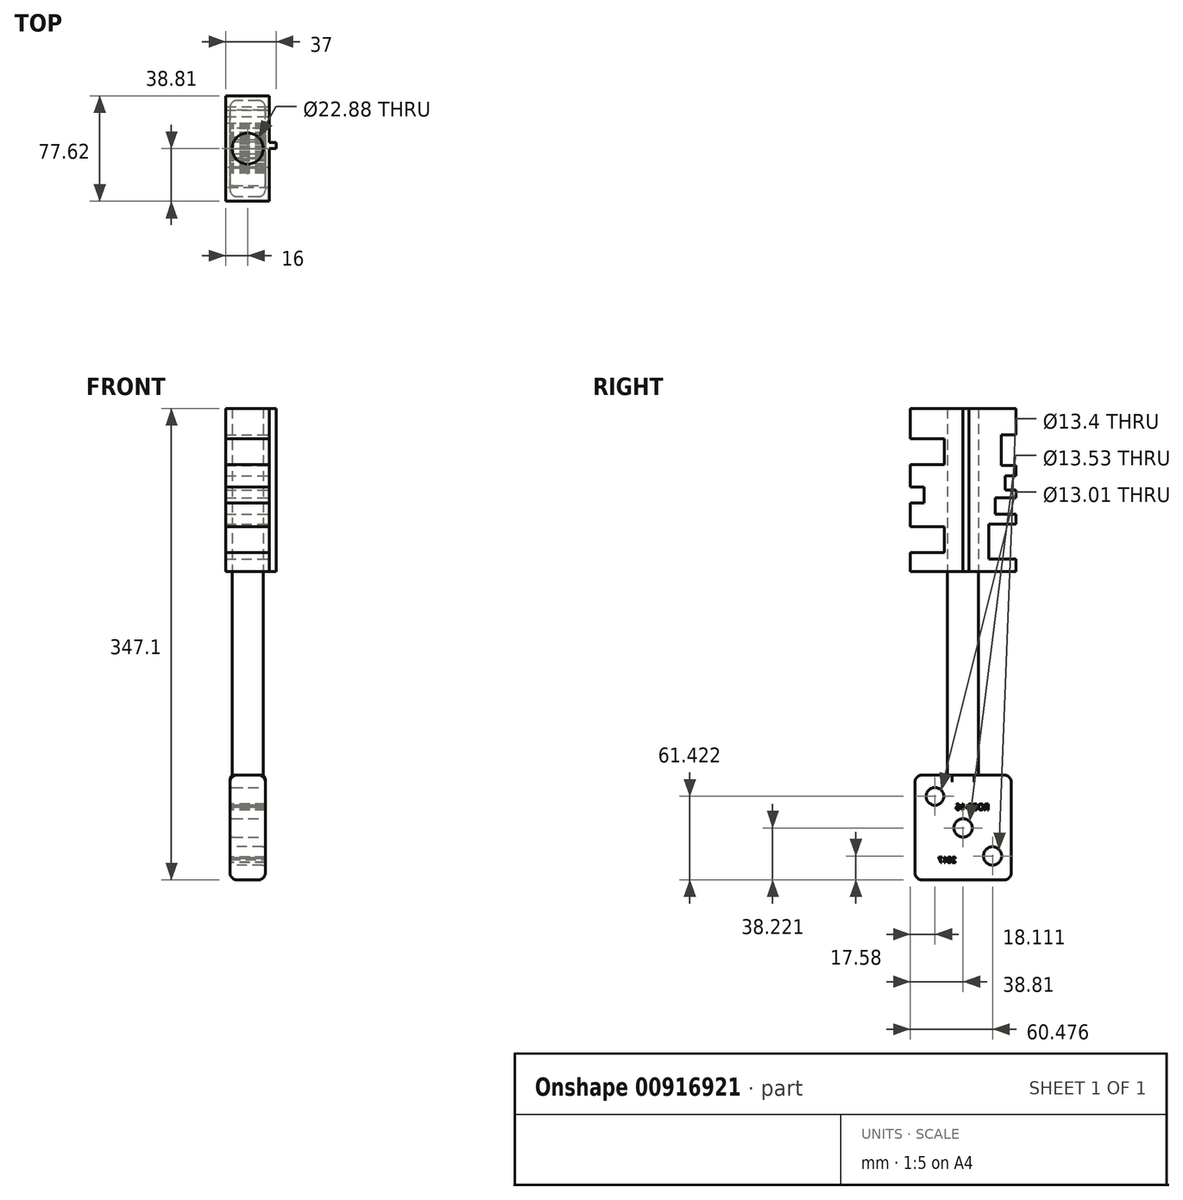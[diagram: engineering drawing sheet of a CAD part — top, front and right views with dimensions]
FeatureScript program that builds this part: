
annotation { "Feature Type Name" : "Feature", "Feature Type Description" : "" }
export const myFeature = defineFeature(function(context is Context, id is Id, definition is map)
    precondition{}
    {
        {
            var Q0;
            Q0=qCreatedBy(makeId("Top.planeOp"),FACE);
            var sketch = newSketch(context, id + "F0", { "sketchPlane" : qUnion([Q0])});
            skCircle(sketch, "E0", {"center": v(0, 0) * mm, "radius": 11.44 * mm});
            skSolve(sketch);
        }
        {
            var Q0;
            Q0=makeQuery(id+"F0.imprint","IMPRINT",FACE,{"disambiguationData":[TD([[makeQuery(id+"F0.imprint","IMPRINT",EDGE,{"derivedFrom":sQuery(id+"F0.wireOp",EDGE,"E0")}),1.0]])]});
            extrude(context, id + "F1", {"entities" : qUnion([Q0]), "depth" : 150 * mm, "offsetDistance" : 25 * mm});
        }
        {
            var Q0;
            Q0=makeQuery(id+"F1.opExtrude","CAP_FACE",FACE,{"disambiguationData":[OSD([sQuery(id+"F0.wireOp",EDGE,"E0")])],"isStart":false});
            var sketch = newSketch(context, id + "F2", { "sketchPlane" : qUnion([Q0])});
            skLineSegment(sketch, "E1.bottom", {"start": v(-16, 38.81) * mm, "end": v(16, 38.81) * mm});
            skLineSegment(sketch, "E1.top", {"start": v(-16, -38.81) * mm, "end": v(16, -38.81) * mm});
            skLineSegment(sketch, "E1.left", {"start": v(-16, 38.81) * mm, "end": v(-16, -38.81) * mm});
            skLineSegment(sketch, "E1.right", {"start": v(16, 38.81) * mm, "end": v(16, -38.81) * mm});
            skPoint(sketch, "E1.middle", {"position": v(0, 0) * mm});
            skSolve(sketch);
        }
        {
            var Q0;
            Q0=makeQuery(id+"F2.imprint","IMPRINT",FACE,{"disambiguationData":[TD([[makeQuery(id+"F2.imprint","IMPRINT",EDGE,{"derivedFrom":sQuery(id+"F2.wireOp",EDGE,"E1.bottom")}),-1.0]])]});
            extrude(context, id + "F3", {"entities" : qUnion([Q0]), "depth" : 120 * mm, "offsetDistance" : 25 * mm});
        }
        {
            var Q0;
            Q0=makeQuery(id+"F3.opExtrude","SWEPT_FACE",FACE,{"disambiguationData":[OSD([sQuery(id+"F2.wireOp",EDGE,"E1.top")])]});
            var sketch = newSketch(context, id + "F4", { "sketchPlane" : qUnion([Q0])});
            skLineSegment(sketch, "E2.bottom", {"start": v(16, 182.75) * mm, "end": v(-16, 182.75) * mm});
            skLineSegment(sketch, "E2.top", {"start": v(16, 163.99) * mm, "end": v(-16, 163.99) * mm});
            skLineSegment(sketch, "E2.left", {"start": v(16, 182.75) * mm, "end": v(16, 163.99) * mm});
            skLineSegment(sketch, "E2.right", {"start": v(-16, 182.75) * mm, "end": v(-16, 163.99) * mm});
            skPoint(sketch, "E2.middle", {"position": v(0, 173.37) * mm});
            skSolve(sketch);
        }
        {
            var Q0;
            Q0=makeQuery(id+"F4.imprint","IMPRINT",FACE,{"disambiguationData":[TD([[makeQuery(id+"F4.imprint","IMPRINT",EDGE,{"derivedFrom":sQuery(id+"F4.wireOp",EDGE,"E2.bottom")}),1.0]])]});
            extrude(context, id + "F5", {"entities" : qUnion([Q0]), "operationType" : NewBodyOperationType.REMOVE, "oppositeDirection" : true, "depth" : 25 * mm, "offsetDistance" : 25 * mm});
        }
        {
            var Q0;
            {var subQ2=sQuery(id+"F2.wireOp",EDGE,"E1.top");Q0=makeQuery(id+"F5.boolean.opBoolean","SPLIT",FACE,{"disambiguationData":[TD([makeQuery(id+"F5.opExtrude","SWEPT_FACE",FACE,{"disambiguationData":[OSD([sQuery(id+"F4.wireOp",EDGE,"E2.bottom")])]})])],"derivedFrom":makeQuery(id+"F3.opExtrude","SWEPT_FACE",FACE,{"disambiguationData":[OSD([subQ2])]})});}
            var sketch = newSketch(context, id + "F6", { "sketchPlane" : qUnion([Q0])});
            skLineSegment(sketch, "E3.bottom", {"start": v(16, 247.82) * mm, "end": v(-16, 247.82) * mm});
            skLineSegment(sketch, "E3.top", {"start": v(16, 228.54) * mm, "end": v(-16, 228.54) * mm});
            skLineSegment(sketch, "E3.left", {"start": v(16, 247.82) * mm, "end": v(16, 228.54) * mm});
            skLineSegment(sketch, "E3.right", {"start": v(-16, 247.82) * mm, "end": v(-16, 228.54) * mm});
            skPoint(sketch, "E3.middle", {"position": v(0, 238.18) * mm});
            skSolve(sketch);
        }
        {
            var Q0;
            Q0=makeQuery(id+"F6.imprint","IMPRINT",FACE,{"disambiguationData":[TD([[makeQuery(id+"F6.imprint","IMPRINT",EDGE,{"derivedFrom":sQuery(id+"F6.wireOp",EDGE,"E3.bottom")}),1.0]])]});
            extrude(context, id + "F7", {"entities" : qUnion([Q0]), "operationType" : NewBodyOperationType.REMOVE, "oppositeDirection" : true, "depth" : 25 * mm, "offsetDistance" : 25 * mm});
        }
        {
            var Q0;
            {var subQ2=makeQuery(id+"F5.opExtrude","SWEPT_FACE",FACE,{"disambiguationData":[OSD([sQuery(id+"F4.wireOp",EDGE,"E2.bottom")])]});var subQ5=sQuery(id+"F2.wireOp",EDGE,"E1.top");Q0=makeQuery(id+"F7.boolean.opBoolean","SPLIT",FACE,{"disambiguationData":[TD([makeQuery(id+"F5.boolean.opBoolean","COPY",FACE,{"derivedFrom":subQ2})])],"derivedFrom":makeQuery(id+"F5.boolean.opBoolean","SPLIT",FACE,{"disambiguationData":[TD([subQ2])],"derivedFrom":makeQuery(id+"F3.opExtrude","SWEPT_FACE",FACE,{"disambiguationData":[OSD([subQ5])]})})});}
            var sketch = newSketch(context, id + "F8", { "sketchPlane" : qUnion([Q0])});
            skLineSegment(sketch, "E4.bottom", {"start": v(16, 200.25) * mm, "end": v(-16, 200.25) * mm});
            skLineSegment(sketch, "E4.top", {"start": v(16, 212.16) * mm, "end": v(-16, 212.16) * mm});
            skLineSegment(sketch, "E4.left", {"start": v(16, 200.25) * mm, "end": v(16, 212.16) * mm});
            skLineSegment(sketch, "E4.right", {"start": v(-16, 200.25) * mm, "end": v(-16, 212.16) * mm});
            skPoint(sketch, "E4.middle", {"position": v(0, 206.2) * mm});
            skSolve(sketch);
        }
        {
            var Q0;
            Q0=makeQuery(id+"F8.imprint","IMPRINT",FACE,{"disambiguationData":[TD([[makeQuery(id+"F8.imprint","IMPRINT",EDGE,{"derivedFrom":sQuery(id+"F8.wireOp",EDGE,"E4.bottom")}),-1.0]])]});
            extrude(context, id + "F9", {"entities" : qUnion([Q0]), "operationType" : NewBodyOperationType.REMOVE, "oppositeDirection" : true, "depth" : 10 * mm, "offsetDistance" : 25 * mm});
        }
        {
            var Q0;
            Q0=qCreatedBy(makeId("Top.planeOp"),FACE);
            var sketch = newSketch(context, id + "F10", { "sketchPlane" : qUnion([Q0])});
            skLineSegment(sketch, "E5.bottom", {"start": v(12.98, 35.37) * mm, "end": v(-12.98, 35.37) * mm});
            skLineSegment(sketch, "E5.top", {"start": v(12.98, -35.37) * mm, "end": v(-12.98, -35.37) * mm});
            skLineSegment(sketch, "E5.left", {"start": v(12.98, 35.37) * mm, "end": v(12.98, -35.37) * mm});
            skLineSegment(sketch, "E5.right", {"start": v(-12.98, 35.37) * mm, "end": v(-12.98, -35.37) * mm});
            skPoint(sketch, "E5.middle", {"position": v(0, 0) * mm});
            skSolve(sketch);
        }
        {
            var Q0;
            Q0=makeQuery(id+"F10.imprint","IMPRINT",FACE,{"disambiguationData":[TD([[makeQuery(id+"F10.imprint","IMPRINT",EDGE,{"derivedFrom":sQuery(id+"F10.wireOp",EDGE,"E5.bottom")}),1.0]])]});
            extrude(context, id + "F11", {"entities" : qUnion([Q0]), "operationType" : NewBodyOperationType.ADD, "oppositeDirection" : true, "depth" : 77.1 * mm, "offsetDistance" : 25 * mm});
        }
        {
            var Q0;
            Q0=makeQuery(id+"F11.opExtrude","CAP_FACE",FACE,{"disambiguationData":[OSD([sQuery(id+"F10.wireOp",EDGE,"E5.bottom"),sQuery(id+"F10.wireOp",EDGE,"E5.top"),sQuery(id+"F10.wireOp",EDGE,"E5.left"),sQuery(id+"F10.wireOp",EDGE,"E5.right")])],"isStart":false});
            fillet(context, id + "F12", {"entities" : qUnion([Q0]), "radius" : 5 * mm, "tangentPropagation" : true, "allowEdgeOverflow" : false});
        }
        {
            var Q0;
            Q0=makeQuery(id+"F11.opExtrude","SWEPT_FACE",FACE,{"disambiguationData":[OSD([sQuery(id+"F10.wireOp",EDGE,"E5.left")])]});
            var Q1;
            Q1=makeQuery(id+"F11.opExtrude","SWEPT_FACE",FACE,{"disambiguationData":[OSD([sQuery(id+"F10.wireOp",EDGE,"E5.bottom")])]});
            var Q2;
            Q2=makeQuery(id+"F11.opExtrude","SWEPT_FACE",FACE,{"disambiguationData":[OSD([sQuery(id+"F10.wireOp",EDGE,"E5.right")])]});
            var Q3;
            Q3=makeQuery(id+"F11.opExtrude","SWEPT_FACE",FACE,{"disambiguationData":[OSD([sQuery(id+"F10.wireOp",EDGE,"E5.top")])]});
            fillet(context, id + "F13", {"entities" : qUnion([Q0, Q1, Q2, Q3]), "radius" : 5 * mm, "tangentPropagation" : true, "allowEdgeOverflow" : false});
        }
        {
            var Q0;
            Q0=makeQuery(id+"F11.opExtrude","SWEPT_FACE",FACE,{"disambiguationData":[OSD([sQuery(id+"F10.wireOp",EDGE,"E5.right")])]});
            var sketch = newSketch(context, id + "F14", { "sketchPlane" : qUnion([Q0])});
            skCircle(sketch, "E6", {"center": v(-21.67, -59.52) * mm, "radius": 6.7 * mm});
            skSolve(sketch);
        }
        {
            var Q0;
            Q0=makeQuery(id+"F14.imprint","IMPRINT",FACE,{"disambiguationData":[TD([[makeQuery(id+"F14.imprint","IMPRINT",EDGE,{"derivedFrom":sQuery(id+"F14.wireOp",EDGE,"E6")}),1.0]])]});
            extrude(context, id + "F15", {"entities" : qUnion([Q0]), "operationType" : NewBodyOperationType.REMOVE, "oppositeDirection" : true, "depth" : 100000 * mm, "offsetDistance" : 25 * mm});
        }
        {
            var Q0;
            Q0=makeQuery(id+"F11.opExtrude","SWEPT_FACE",FACE,{"disambiguationData":[OSD([sQuery(id+"F10.wireOp",EDGE,"E5.left")])]});
            var sketch = newSketch(context, id + "F16", { "sketchPlane" : qUnion([Q0])});
            skCircle(sketch, "E7", {"center": v(0, -38.88) * mm, "radius": 6.77 * mm});
            skSolve(sketch);
        }
        {
            var Q0;
            Q0=makeQuery(id+"F16.imprint","IMPRINT",FACE,{"disambiguationData":[TD([[makeQuery(id+"F16.imprint","IMPRINT",EDGE,{"derivedFrom":sQuery(id+"F16.wireOp",EDGE,"E7")}),1.0]])]});
            extrude(context, id + "F17", {"entities" : qUnion([Q0]), "operationType" : NewBodyOperationType.REMOVE, "oppositeDirection" : true, "depth" : 100000 * mm, "offsetDistance" : 25 * mm});
        }
        {
            var Q0;
            Q0=makeQuery(id+"F11.opExtrude","SWEPT_FACE",FACE,{"disambiguationData":[OSD([sQuery(id+"F10.wireOp",EDGE,"E5.left")])]});
            var sketch = newSketch(context, id + "F18", { "sketchPlane" : qUnion([Q0])});
            skCircle(sketch, "E8", {"center": v(-20.7, -15.68) * mm, "radius": 6.5 * mm});
            skSolve(sketch);
        }
        {
            var Q0;
            Q0=makeQuery(id+"F18.imprint","IMPRINT",FACE,{"disambiguationData":[TD([[makeQuery(id+"F18.imprint","IMPRINT",EDGE,{"derivedFrom":sQuery(id+"F18.wireOp",EDGE,"E8")}),1.0]])]});
            extrude(context, id + "F19", {"entities" : qUnion([Q0]), "operationType" : NewBodyOperationType.REMOVE, "oppositeDirection" : true, "depth" : 100300 * mm, "offsetDistance" : 25 * mm});
        }
        {
            var Q0;
            Q0=makeQuery(id+"F11.opExtrude","SWEPT_FACE",FACE,{"disambiguationData":[OSD([sQuery(id+"F10.wireOp",EDGE,"E5.right")])]});
            var sketch = newSketch(context, id + "F20", { "sketchPlane" : qUnion([Q0])});
            skText(sketch, "E9", { "text": "ROB9-16", "fontName": "OpenSans-Regular.ttf"});
            skText(sketch, "E10", { "text": "2017", "fontName": "OpenSans-Regular.ttf"});
            const initialGuessF20  = {"E9": [-0.01917, -0.02555, 1, 0, 0.00434], "E10": [0.00512, -0.0645, 1, 0, 0.00416]};
            skSetInitialGuess(sketch, initialGuessF20);
            skSolve(sketch);
        }
        {
            var Q0;
            Q0 = qSketchRegion(id + "F20", true);
            extrude(context, id + "F21", {"entities" : qUnion([Q0]), "operationType" : NewBodyOperationType.REMOVE, "oppositeDirection" : true, "depth" : 100000 * mm, "offsetDistance" : 25 * mm});
        }
        {
            var Q0;
            Q0=makeQuery(id+"F3.opExtrude","SWEPT_FACE",FACE,{"disambiguationData":[OSD([sQuery(id+"F2.wireOp",EDGE,"E1.right")])]});
            var sketch = newSketch(context, id + "F22", { "sketchPlane" : qUnion([Q0])});
            skLineSegment(sketch, "E11.bottom", {"start": v(4.4, 270) * mm, "end": v(0, 270) * mm});
            skLineSegment(sketch, "E11.top", {"start": v(4.4, 150) * mm, "end": v(0, 150) * mm});
            skLineSegment(sketch, "E11.left", {"start": v(4.4, 270) * mm, "end": v(4.4, 150) * mm});
            skLineSegment(sketch, "E11.right", {"start": v(0, 270) * mm, "end": v(0, 150) * mm});
            skSolve(sketch);
        }
        {
            var Q0;
            Q0=makeQuery(id+"F22.imprint","IMPRINT",FACE,{"disambiguationData":[TD([[makeQuery(id+"F22.imprint","IMPRINT",EDGE,{"derivedFrom":sQuery(id+"F22.wireOp",EDGE,"E11.bottom")}),1.0]])]});
            extrude(context, id + "F23", {"entities" : qUnion([Q0]), "operationType" : NewBodyOperationType.ADD, "depth" : 5 * mm, "offsetDistance" : 25 * mm});
        }
        {
            var Q0;
            {var subQ0=sQuery(id+"F2.wireOp",EDGE,"E1.right");var subQ3=sQuery(id+"F2.wireOp",EDGE,"E1.bottom");Q0=makeQuery(id+"F23.boolean.opBoolean","SPLIT",FACE,{"disambiguationData":[TD([makeQuery(id+"F3.opExtrude","SWEPT_FACE",FACE,{"disambiguationData":[OSD([subQ3])]})])],"derivedFrom":makeQuery(id+"F3.opExtrude","SWEPT_FACE",FACE,{"disambiguationData":[OSD([subQ0])]})});}
            var sketch = newSketch(context, id + "F24", { "sketchPlane" : qUnion([Q0])});
            skLineSegment(sketch, "E12.bottom", {"start": v(38.81, 250.4) * mm, "end": v(28.19, 250.4) * mm});
            skLineSegment(sketch, "E12.top", {"start": v(38.81, 228.1) * mm, "end": v(28.19, 228.1) * mm});
            skLineSegment(sketch, "E12.left", {"start": v(38.81, 250.4) * mm, "end": v(38.81, 228.1) * mm});
            skLineSegment(sketch, "E12.right", {"start": v(28.19, 250.4) * mm, "end": v(28.19, 228.1) * mm});
            skSolve(sketch);
        }
        {
            var Q0;
            Q0=makeQuery(id+"F24.imprint","IMPRINT",FACE,{"disambiguationData":[TD([[makeQuery(id+"F24.imprint","IMPRINT",EDGE,{"derivedFrom":sQuery(id+"F24.wireOp",EDGE,"E12.bottom")}),1.0]])]});
            extrude(context, id + "F25", {"entities" : qUnion([Q0]), "operationType" : NewBodyOperationType.REMOVE, "oppositeDirection" : true, "depth" : 100300 * mm, "offsetDistance" : 25 * mm});
        }
        {
            var Q0;
            {var subQ0=sQuery(id+"F2.wireOp",EDGE,"E1.right");var subQ3=sQuery(id+"F2.wireOp",EDGE,"E1.bottom");Q0=makeQuery(id+"F23.boolean.opBoolean","SPLIT",FACE,{"disambiguationData":[TD([makeQuery(id+"F3.opExtrude","SWEPT_FACE",FACE,{"disambiguationData":[OSD([subQ3])]})])],"derivedFrom":makeQuery(id+"F3.opExtrude","SWEPT_FACE",FACE,{"disambiguationData":[OSD([subQ0])]})});}
            var sketch = newSketch(context, id + "F26", { "sketchPlane" : qUnion([Q0])});
            skPoint(sketch, "E13.oppositeSnap0", {"position": v(4.4, 210) * mm});
            skLineSegment(sketch, "E13.bottom", {"start": v(38.81, 220.4) * mm, "end": v(30.93, 220.4) * mm});
            skLineSegment(sketch, "E13.top", {"start": v(38.81, 210) * mm, "end": v(30.93, 210) * mm});
            skLineSegment(sketch, "E13.left", {"start": v(38.81, 220.4) * mm, "end": v(38.81, 210) * mm});
            skLineSegment(sketch, "E13.right", {"start": v(30.93, 220.4) * mm, "end": v(30.93, 210) * mm});
            skSolve(sketch);
        }
        {
            var Q0;
            Q0=makeQuery(id+"F26.imprint","IMPRINT",FACE,{"disambiguationData":[TD([[makeQuery(id+"F26.imprint","IMPRINT",EDGE,{"derivedFrom":sQuery(id+"F26.wireOp",EDGE,"E13.bottom")}),1.0]])]});
            extrude(context, id + "F27", {"entities" : qUnion([Q0]), "operationType" : NewBodyOperationType.REMOVE, "oppositeDirection" : true, "depth" : 90 * mm, "offsetDistance" : 25 * mm});
        }
        {
            var Q0;
            {var subQ0=sQuery(id+"F2.wireOp",EDGE,"E1.right");var subQ3=sQuery(id+"F2.wireOp",EDGE,"E1.bottom");Q0=makeQuery(id+"F23.boolean.opBoolean","SPLIT",FACE,{"disambiguationData":[TD([makeQuery(id+"F3.opExtrude","SWEPT_FACE",FACE,{"disambiguationData":[OSD([subQ3])]})])],"derivedFrom":makeQuery(id+"F3.opExtrude","SWEPT_FACE",FACE,{"disambiguationData":[OSD([subQ0])]})});}
            var sketch = newSketch(context, id + "F28", { "sketchPlane" : qUnion([Q0])});
            skLineSegment(sketch, "E14.bottom", {"start": v(23.68, 192.18) * mm, "end": v(38.81, 192.18) * mm});
            skLineSegment(sketch, "E14.top", {"start": v(23.68, 204.21) * mm, "end": v(38.81, 204.21) * mm});
            skLineSegment(sketch, "E14.left", {"start": v(23.68, 192.18) * mm, "end": v(23.68, 204.21) * mm});
            skLineSegment(sketch, "E14.right", {"start": v(38.81, 192.18) * mm, "end": v(38.81, 204.21) * mm});
            skSolve(sketch);
        }
        {
            var Q0;
            Q0=makeQuery(id+"F28.imprint","IMPRINT",FACE,{"disambiguationData":[TD([[makeQuery(id+"F28.imprint","IMPRINT",EDGE,{"derivedFrom":sQuery(id+"F28.wireOp",EDGE,"E14.bottom")}),1.0]])]});
            extrude(context, id + "F29", {"entities" : qUnion([Q0]), "operationType" : NewBodyOperationType.REMOVE, "oppositeDirection" : true, "depth" : 90 * mm, "offsetDistance" : 25 * mm});
        }
        {
            var Q0;
            {var subQ0=sQuery(id+"F2.wireOp",EDGE,"E1.right");var subQ3=sQuery(id+"F2.wireOp",EDGE,"E1.bottom");Q0=makeQuery(id+"F23.boolean.opBoolean","SPLIT",FACE,{"disambiguationData":[TD([makeQuery(id+"F3.opExtrude","SWEPT_FACE",FACE,{"disambiguationData":[OSD([subQ3])]})])],"derivedFrom":makeQuery(id+"F3.opExtrude","SWEPT_FACE",FACE,{"disambiguationData":[OSD([subQ0])]})});}
            var sketch = newSketch(context, id + "F30", { "sketchPlane" : qUnion([Q0])});
            skLineSegment(sketch, "E15.bottom", {"start": v(38.81, 159.07) * mm, "end": v(18.85, 159.07) * mm});
            skLineSegment(sketch, "E15.top", {"start": v(38.81, 184.72) * mm, "end": v(18.85, 184.72) * mm});
            skLineSegment(sketch, "E15.left", {"start": v(38.81, 159.07) * mm, "end": v(38.81, 184.72) * mm});
            skLineSegment(sketch, "E15.right", {"start": v(18.85, 159.07) * mm, "end": v(18.85, 184.72) * mm});
            skSolve(sketch);
        }
        {
            var Q0;
            Q0=makeQuery(id+"F30.imprint","IMPRINT",FACE,{"disambiguationData":[TD([[makeQuery(id+"F30.imprint","IMPRINT",EDGE,{"derivedFrom":sQuery(id+"F30.wireOp",EDGE,"E15.bottom")}),-1.0]])]});
            extrude(context, id + "F31", {"entities" : qUnion([Q0]), "operationType" : NewBodyOperationType.REMOVE, "oppositeDirection" : true, "depth" : 90 * mm, "offsetDistance" : 25 * mm});
        }
        {
            var Q0;
            Q0=makeQuery(id+"F17.boolean.opBoolean","INTERSECT",EDGE,{"derivedFrom":[makeQuery(id+"F11.opExtrude","SWEPT_FACE",FACE,{"disambiguationData":[OSD([sQuery(id+"F10.wireOp",EDGE,"E5.right")])]}),makeQuery(id+"F17.opExtrude","SWEPT_FACE",FACE,{"disambiguationData":[OSD([sQuery(id+"F16.wireOp",EDGE,"E7")])]})]});
            var Q1;
            Q1=makeQuery(id+"F17.boolean.opBoolean","COPY",EDGE,{"derivedFrom":makeQuery(id+"F17.opExtrude","CAP_EDGE",EDGE,{"disambiguationData":[OSD([sQuery(id+"F16.wireOp",EDGE,"E7")])],"isStart":true})});
            var Q2;
            Q2=makeQuery(id+"F15.boolean.opBoolean","COPY",EDGE,{"derivedFrom":makeQuery(id+"F15.opExtrude","CAP_EDGE",EDGE,{"disambiguationData":[OSD([sQuery(id+"F14.wireOp",EDGE,"E6")])],"isStart":true})});
            var Q3;
            Q3=makeQuery(id+"F15.boolean.opBoolean","INTERSECT",EDGE,{"derivedFrom":[makeQuery(id+"F11.opExtrude","SWEPT_FACE",FACE,{"disambiguationData":[OSD([sQuery(id+"F10.wireOp",EDGE,"E5.left")])]}),makeQuery(id+"F15.opExtrude","SWEPT_FACE",FACE,{"disambiguationData":[OSD([sQuery(id+"F14.wireOp",EDGE,"E6")])]})]});
            var Q4;
            Q4=makeQuery(id+"F19.boolean.opBoolean","COPY",EDGE,{"derivedFrom":makeQuery(id+"F19.opExtrude","CAP_EDGE",EDGE,{"disambiguationData":[OSD([sQuery(id+"F18.wireOp",EDGE,"E8")])],"isStart":true})});
            var Q5;
            Q5=makeQuery(id+"F19.boolean.opBoolean","INTERSECT",EDGE,{"derivedFrom":[makeQuery(id+"F11.opExtrude","SWEPT_FACE",FACE,{"disambiguationData":[OSD([sQuery(id+"F10.wireOp",EDGE,"E5.right")])]}),makeQuery(id+"F19.opExtrude","SWEPT_FACE",FACE,{"disambiguationData":[OSD([sQuery(id+"F18.wireOp",EDGE,"E8")])]})]});
            fillet(context, id + "F32", {"entities" : qUnion([Q0, Q1, Q2, Q3, Q4, Q5]), "radius" : 2 * mm, "tangentPropagation" : true, "allowEdgeOverflow" : false});
        }
    });
